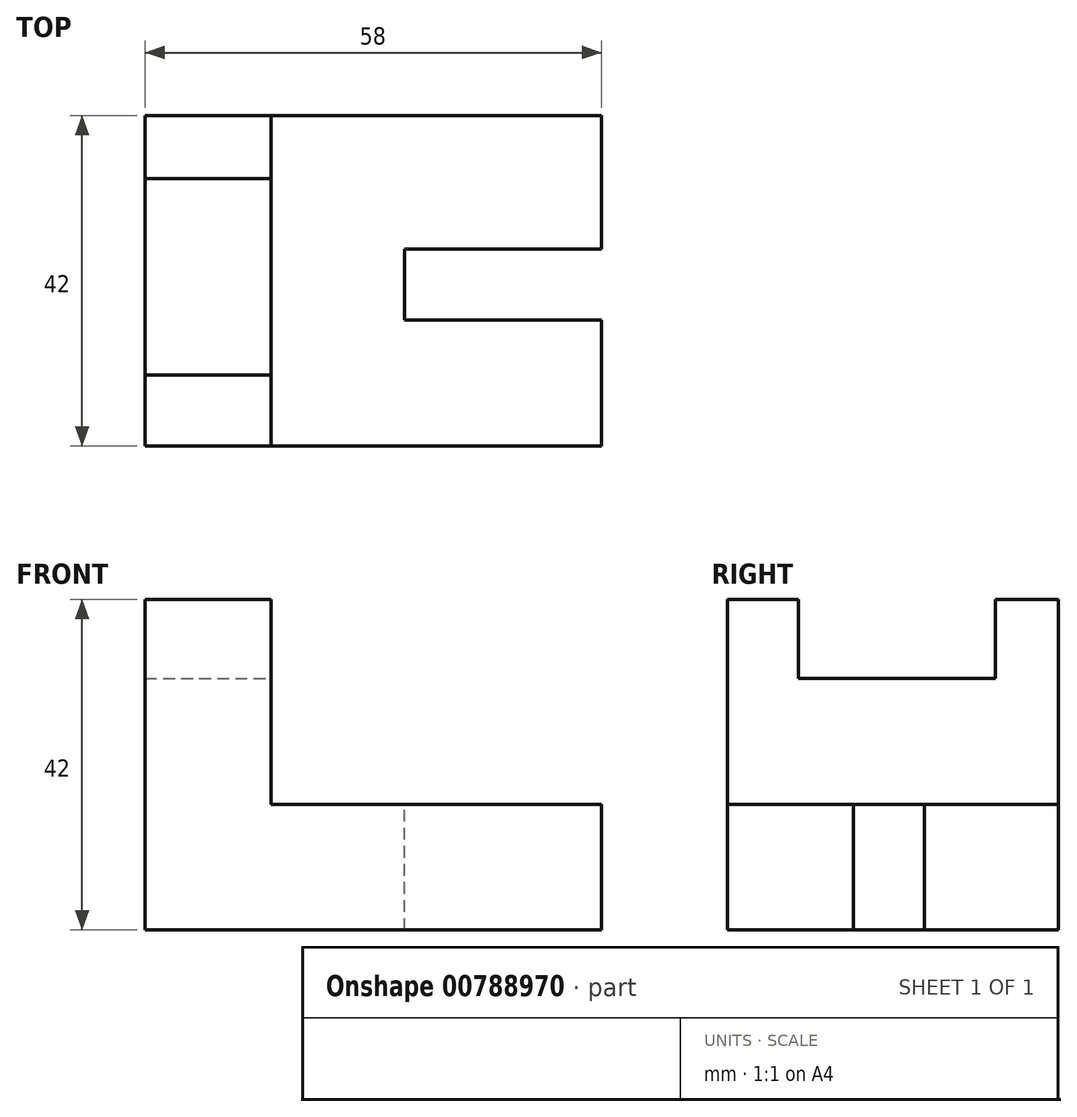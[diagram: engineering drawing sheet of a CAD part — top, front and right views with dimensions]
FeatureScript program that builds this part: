
annotation { "Feature Type Name" : "Feature", "Feature Type Description" : "" }
export const myFeature = defineFeature(function(context is Context, id is Id, definition is map)
    precondition{}
    {
        {
            var Q0;
            Q0=qCreatedBy(makeId("Front.planeOp"),FACE);
            var sketch = newSketch(context, id + "F0", { "sketchPlane" : qUnion([Q0])});
            skLineSegment(sketch, "E0", {"start": v(0, 0) * mm, "end": v(0, 42) * mm});
            skLineSegment(sketch, "E1", {"start": v(0, 42) * mm, "end": v(16, 42) * mm});
            skLineSegment(sketch, "E2", {"start": v(16, 42) * mm, "end": v(16, 16) * mm});
            skLineSegment(sketch, "E3", {"start": v(16, 16) * mm, "end": v(58, 16) * mm});
            skLineSegment(sketch, "E4", {"start": v(58, 16) * mm, "end": v(58, 0) * mm});
            skLineSegment(sketch, "E5", {"start": v(58, 0) * mm, "end": v(0, 0) * mm});
            skSolve(sketch);
        }
        {
            var Q0;
            Q0=makeQuery(id+"F0.imprint","IMPRINT",FACE,{"disambiguationData":[TD([[makeQuery(id+"F0.imprint","IMPRINT",EDGE,{"derivedFrom":sQuery(id+"F0.wireOp",EDGE,"E0")}),-1.0]])]});
            extrude(context, id + "F1", {"entities" : qUnion([Q0]), "depth" : 42 * mm, "offsetDistance" : 25 * mm});
        }
        {
            var Q0;
            Q0=makeQuery(id+"F1.opExtrude","SWEPT_FACE",FACE,{"disambiguationData":[OSD([sQuery(id+"F0.wireOp",EDGE,"E1")])]});
            var sketch = newSketch(context, id + "F2", { "sketchPlane" : qUnion([Q0])});
            skLineSegment(sketch, "E6.bottom", {"start": v(0, -8) * mm, "end": v(16, -8) * mm});
            skLineSegment(sketch, "E6.top", {"start": v(0, -33) * mm, "end": v(16, -33) * mm});
            skLineSegment(sketch, "E6.left", {"start": v(0, -8) * mm, "end": v(0, -33) * mm});
            skLineSegment(sketch, "E6.right", {"start": v(16, -8) * mm, "end": v(16, -33) * mm});
            skSolve(sketch);
        }
        {
            var Q0;
            Q0=makeQuery(id+"F2.imprint","IMPRINT",FACE,{"disambiguationData":[TD([[makeQuery(id+"F2.imprint","IMPRINT",EDGE,{"derivedFrom":sQuery(id+"F2.wireOp",EDGE,"E6.bottom")}),-1.0]])]});
            extrude(context, id + "F3", {"entities" : qUnion([Q0]), "operationType" : NewBodyOperationType.REMOVE, "oppositeDirection" : true, "depth" : 10 * mm, "offsetDistance" : 25 * mm});
        }
        {
            var Q0;
            Q0=makeQuery(id+"F1.opExtrude","SWEPT_FACE",FACE,{"disambiguationData":[OSD([sQuery(id+"F0.wireOp",EDGE,"E3")])]});
            var sketch = newSketch(context, id + "F4", { "sketchPlane" : qUnion([Q0])});
            skLineSegment(sketch, "E7.bottom", {"start": v(58, -17) * mm, "end": v(33, -17) * mm});
            skLineSegment(sketch, "E7.top", {"start": v(58, -26) * mm, "end": v(33, -26) * mm});
            skLineSegment(sketch, "E7.left", {"start": v(58, -17) * mm, "end": v(58, -26) * mm});
            skLineSegment(sketch, "E7.right", {"start": v(33, -17) * mm, "end": v(33, -26) * mm});
            skSolve(sketch);
        }
        {
            var Q0;
            Q0=makeQuery(id+"F4.imprint","IMPRINT",FACE,{"disambiguationData":[TD([[makeQuery(id+"F4.imprint","IMPRINT",EDGE,{"derivedFrom":sQuery(id+"F4.wireOp",EDGE,"E7.bottom")}),1.0]])]});
            extrude(context, id + "F5", {"entities" : qUnion([Q0]), "operationType" : NewBodyOperationType.REMOVE, "endBound" : BoundingType.THROUGH_ALL, "oppositeDirection" : true, "depth" : 25 * mm, "offsetDistance" : 25 * mm});
        }
    });
